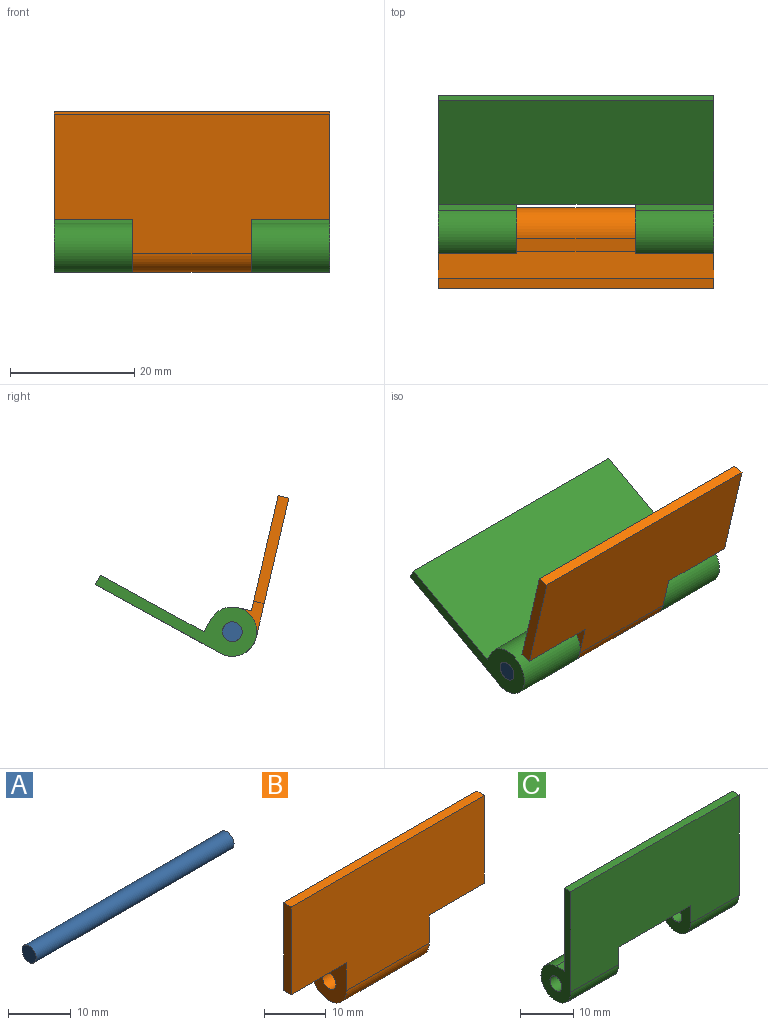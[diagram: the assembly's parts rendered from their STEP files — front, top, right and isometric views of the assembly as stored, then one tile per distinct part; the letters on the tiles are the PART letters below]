
ASSEMBLY  parts=3 mates=4
PART A: 3 faces, bbox 44.5x3.2x3.2 mm
  f0: cylinder r=1.59mm len=44.45mm, axis (-1,0,0), area 443.4mm2, adj f1,f2
  f1: plane 3.18x3.18mm, normal (1,0,0), area 7.9mm2, adj f0
  f2: plane 3.18x3.18mm, normal (-1,0,0), area 7.9mm2, adj f0
PART B: 12 faces, bbox 44.5x7.9x27 mm
  f0: plane 9.53x7.94mm, normal (-1,0,0), area 47.7mm2, adj f1,f2,f4,f9,f10,f11
  f1: plane 44.45x23.02mm, normal (0,-1,0), area 882.1mm2, adj f0,f3,f4,f5,f6,f7,f8,f11
  f2: plane 19.05x2.22mm, normal (0,0,1), area 42.3mm2, adj f0,f5,f9,f11
  f3: plane 17.46x1.75mm, normal (-1,0,0), area 30.6mm2, adj f1,f4,f8,f9
  f4: plane 12.7x1.75mm, normal (0,0,-1), area 22.2mm2, adj f0,f1,f3,f9
  f5: plane 9.53x7.94mm, normal (1,0,0), area 47.7mm2, adj f1,f2,f6,f9,f10,f11
  f6: plane 12.7x1.75mm, normal (0,0,-1), area 22.2mm2, adj f1,f5,f7,f9
  f7: plane 17.46x1.75mm, normal (1,0,0), area 30.6mm2, adj f1,f6,f8,f9
  f8: plane 44.45x1.75mm, normal (0,0,1), area 77.8mm2, adj f1,f3,f7,f9
  f9: plane 44.45x19.05mm, normal (0,1,0), area 806.4mm2, adj f0,f2,f3,f4,f5,f6,f7,f8
  f10: cylinder r=1.59mm len=19.05mm, axis (1,0,0), area 190mm2, adj f0,f5
  f11: cylinder r=3.97mm len=19.05mm, axis (1,0,0), area 356.3mm2, adj f0,f1,f2,f5
PART C: 14 faces, bbox 44.5x7.9x27 mm
  f0: plane 26.99x7.94mm, normal (1,0,0), area 78.3mm2, adj f4,f5,f8,f9,f11,f13
  f1: plane 26.99x7.94mm, normal (-1,0,0), area 78.3mm2, adj f4,f6,f8,f9,f10,f12
  f2: plane 7.94x7.94mm, normal (-1,0,0), area 44.9mm2, adj f4,f5,f7,f11,f13
  f3: plane 7.94x7.94mm, normal (1,0,0), area 44.9mm2, adj f4,f6,f7,f10,f12
  f4: plane 44.45x23.02mm, normal (0,-1,0), area 947.6mm2, adj f0,f1,f2,f3,f7,f8,f10,f11
  f5: plane 12.7x2.22mm, normal (0,0,1), area 28.2mm2, adj f0,f2,f9,f11
  f6: plane 12.7x2.22mm, normal (0,0,1), area 28.2mm2, adj f1,f3,f9,f10
  f7: plane 19.05x1.75mm, normal (0,0,-1), area 33.3mm2, adj f2,f3,f4,f9
  f8: plane 44.45x1.75mm, normal (0,0,1), area 77.8mm2, adj f0,f1,f4,f9
  f9: plane 44.45x19.05mm, normal (0,1,0), area 846.8mm2, adj f0,f1,f5,f6,f7,f8
  f10: cylinder r=3.97mm len=12.7mm, axis (1,0,0), area 237.5mm2, adj f1,f3,f4,f6
  f11: cylinder r=3.97mm len=12.7mm, axis (1,0,0), area 237.5mm2, adj f0,f2,f4,f5
  f12: cylinder r=1.59mm len=12.7mm, axis (1,0,0), area 126.7mm2, adj f1,f3
  f13: cylinder r=1.59mm len=12.7mm, axis (1,0,0), area 126.7mm2, adj f0,f2
PLACE A rot(axis=(1,0,0),123.2deg) t=(-17.85,-9.32,3.77)mm
PLACE B rot(axis=(1,0,0),13.2deg) t=(-17.85,-14.09,6.74)mm fixed
PLACE C rot(axis=(0,-0.51,-0.86),180deg) t=(26.6,-3.94,2.2)mm
MATE planar A.f0 <-> C.f1  axis (1,0,0) through (26.6,-9.32,3.77)mm
MATE cylindrical A.f0 <-> B.f10  axis (-1,0,0) through (4.37,-9.32,3.77)mm
MATE planar B.f5 <-> C.f10  axis (1,0,0) through (13.9,-9.82,4.17)mm
MATE cylindrical A.f0 <-> C.f10  axis (-1,0,0) through (4.37,-9.32,3.77)mm
